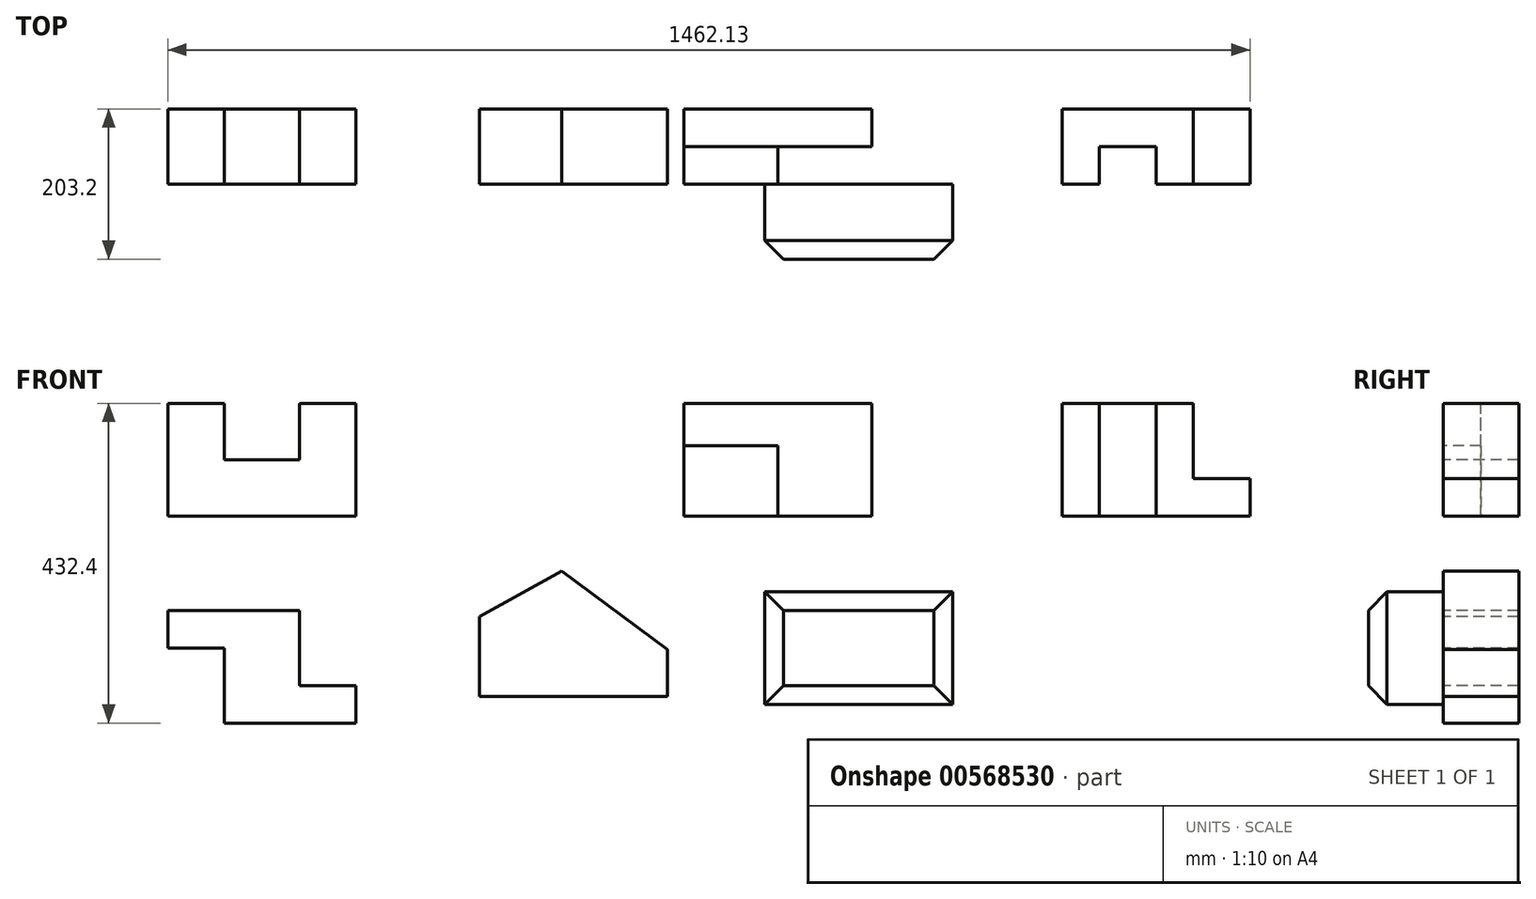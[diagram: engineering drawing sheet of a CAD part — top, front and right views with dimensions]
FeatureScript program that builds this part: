
annotation { "Feature Type Name" : "Feature", "Feature Type Description" : "" }
export const myFeature = defineFeature(function(context is Context, id is Id, definition is map)
    precondition{}
    {
        {
            var Q0;
            Q0=qCreatedBy(makeId("Front.planeOp"),FACE);
            var sketch = newSketch(context, id + "F0", { "sketchPlane" : qUnion([Q0])});
            skLineSegment(sketch, "E0", {"start": v(0, 0) * mm, "end": v(254, 0) * mm});
            skLineSegment(sketch, "E1", {"start": v(254, 0) * mm, "end": v(254, 152.4) * mm});
            skLineSegment(sketch, "E2", {"start": v(254, 152.4) * mm, "end": v(177.8, 152.4) * mm});
            skLineSegment(sketch, "E3", {"start": v(177.8, 152.4) * mm, "end": v(177.8, 76.2) * mm});
            skLineSegment(sketch, "E4", {"start": v(177.8, 76.2) * mm, "end": v(76.2, 76.2) * mm});
            skLineSegment(sketch, "E5", {"start": v(76.2, 76.2) * mm, "end": v(76.2, 152.4) * mm});
            skLineSegment(sketch, "E6", {"start": v(76.2, 152.4) * mm, "end": v(0, 152.4) * mm});
            skLineSegment(sketch, "E7", {"start": v(0, 152.4) * mm, "end": v(0, 0) * mm});
            skSolve(sketch);
        }
        {
            var Q0;
            Q0=makeQuery(id+"F0.imprint","IMPRINT",FACE,{"disambiguationData":[TD([[makeQuery(id+"F0.imprint","IMPRINT",EDGE,{"derivedFrom":sQuery(id+"F0.wireOp",EDGE,"E0")}),1.0]])]});
            extrude(context, id + "F1", {"entities" : qUnion([Q0]), "oppositeDirection" : true, "depth" : 101.6 * mm, "offsetDistance" : 25.4 * mm});
        }
        {
            var Q0;
            Q0=qCreatedBy(makeId("Front.planeOp"),FACE);
            var sketch = newSketch(context, id + "F2", { "sketchPlane" : qUnion([Q0])});
            skLineSegment(sketch, "E8.bottom", {"start": v(697.05, 0) * mm, "end": v(951.05, 0) * mm});
            skLineSegment(sketch, "E8.top", {"start": v(697.05, 152.4) * mm, "end": v(951.05, 152.4) * mm});
            skLineSegment(sketch, "E8.left", {"start": v(697.05, 0) * mm, "end": v(697.05, 152.4) * mm});
            skLineSegment(sketch, "E8.right", {"start": v(951.05, 0) * mm, "end": v(951.05, 152.4) * mm});
            skSolve(sketch);
        }
        {
            var Q0;
            Q0=makeQuery(id+"F2.imprint","IMPRINT",FACE,{"disambiguationData":[TD([[makeQuery(id+"F2.imprint","IMPRINT",EDGE,{"derivedFrom":sQuery(id+"F2.wireOp",EDGE,"E8.bottom")}),1.0]])]});
            extrude(context, id + "F3", {"entities" : qUnion([Q0]), "oppositeDirection" : true, "depth" : 101.6 * mm, "offsetDistance" : 25.4 * mm});
        }
        {
            var Q0;
            Q0=makeQuery(id+"F3.opExtrude","CAP_FACE",FACE,{"disambiguationData":[OSD([sQuery(id+"F2.wireOp",EDGE,"E8.bottom"),sQuery(id+"F2.wireOp",EDGE,"E8.top"),sQuery(id+"F2.wireOp",EDGE,"E8.left"),sQuery(id+"F2.wireOp",EDGE,"E8.right")])],"isStart":true});
            var sketch = newSketch(context, id + "F4", { "sketchPlane" : qUnion([Q0])});
            skLineSegment(sketch, "E9", {"start": v(951.05, 0) * mm, "end": v(951.05, 152.4) * mm});
            skLineSegment(sketch, "E10", {"start": v(951.05, 152.4) * mm, "end": v(697.05, 152.4) * mm});
            skLineSegment(sketch, "E11", {"start": v(824.05, 101.6) * mm, "end": v(824.05, 0) * mm});
            skLineSegment(sketch, "E12", {"start": v(697.05, 95.19) * mm, "end": v(824.05, 95.19) * mm});
            skSolve(sketch);
        }
        {
            var Q0;
            {var subQ5=sQuery(id+"F4.wireOp",EDGE,"E9");Q0=makeQuery(id+"F4.imprint","IMPRINT",FACE,{"disambiguationData":[TD([[makeQuery(id+"F4.imprint","IMPRINT",EDGE,{"derivedFrom":subQ5}),1.0]])]});}
            extrude(context, id + "F5", {"entities" : qUnion([Q0]), "operationType" : NewBodyOperationType.REMOVE, "oppositeDirection" : true, "depth" : 50.8 * mm, "offsetDistance" : 25.4 * mm});
        }
        {
            var Q0;
            Q0=qCreatedBy(makeId("Front.planeOp"),FACE);
            var sketch = newSketch(context, id + "F6", { "sketchPlane" : qUnion([Q0])});
            skLineSegment(sketch, "E13", {"start": v(1208.13, 0) * mm, "end": v(1462.13, 0) * mm});
            skLineSegment(sketch, "E14", {"start": v(1462.13, 0) * mm, "end": v(1462.13, 50.8) * mm});
            skLineSegment(sketch, "E15", {"start": v(1462.13, 50.8) * mm, "end": v(1385.93, 50.8) * mm});
            skLineSegment(sketch, "E16", {"start": v(1385.93, 50.8) * mm, "end": v(1385.93, 152.4) * mm});
            skLineSegment(sketch, "E17", {"start": v(1385.93, 152.4) * mm, "end": v(1208.13, 152.4) * mm});
            skLineSegment(sketch, "E18", {"start": v(1208.13, 152.4) * mm, "end": v(1208.13, 0) * mm});
            skSolve(sketch);
        }
        {
            var Q0;
            Q0=makeQuery(id+"F6.imprint","IMPRINT",FACE,{"disambiguationData":[TD([[makeQuery(id+"F6.imprint","IMPRINT",EDGE,{"derivedFrom":sQuery(id+"F6.wireOp",EDGE,"E13")}),1.0]])]});
            extrude(context, id + "F7", {"entities" : qUnion([Q0]), "oppositeDirection" : true, "depth" : 101.6 * mm, "offsetDistance" : 25.4 * mm});
        }
        {
            var Q0;
            Q0=makeQuery(id+"F7.opExtrude","SWEPT_FACE",FACE,{"disambiguationData":[OSD([sQuery(id+"F6.wireOp",EDGE,"E17")])]});
            var sketch = newSketch(context, id + "F8", { "sketchPlane" : qUnion([Q0])});
            skLineSegment(sketch, "E19", {"start": v(1208.13, 0) * mm, "end": v(1258.93, 0) * mm});
            skLineSegment(sketch, "E20", {"start": v(1258.93, 0) * mm, "end": v(1258.93, 50.8) * mm});
            skLineSegment(sketch, "E21", {"start": v(1258.93, 50.8) * mm, "end": v(1335.13, 50.8) * mm});
            skLineSegment(sketch, "E22", {"start": v(1335.13, 50.8) * mm, "end": v(1335.13, 0) * mm});
            skLineSegment(sketch, "E23", {"start": v(1335.13, 0) * mm, "end": v(1258.93, 0) * mm});
            skSolve(sketch);
        }
        {
            var Q0;
            Q0=makeQuery(id+"F8.imprint","IMPRINT",FACE,{"disambiguationData":[TD([[makeQuery(id+"F8.imprint","IMPRINT",EDGE,{"derivedFrom":sQuery(id+"F8.wireOp",EDGE,"E20")}),-1.0]])]});
            extrude(context, id + "F9", {"entities" : qUnion([Q0]), "operationType" : NewBodyOperationType.REMOVE, "oppositeDirection" : true, "depth" : 152.4 * mm, "offsetDistance" : 25.4 * mm});
        }
        {
            var Q0;
            Q0=qCreatedBy(makeId("Front.planeOp"),FACE);
            var sketch = newSketch(context, id + "F10", { "sketchPlane" : qUnion([Q0])});
            skLineSegment(sketch, "E24", {"start": v(0, -178.4) * mm, "end": v(76.2, -178.4) * mm});
            skLineSegment(sketch, "E25", {"start": v(76.2, -178.4) * mm, "end": v(76.2, -280) * mm});
            skLineSegment(sketch, "E26", {"start": v(76.2, -280) * mm, "end": v(254, -280) * mm});
            skLineSegment(sketch, "E27", {"start": v(254, -280) * mm, "end": v(254, -229.2) * mm});
            skLineSegment(sketch, "E28", {"start": v(254, -229.2) * mm, "end": v(177.8, -229.2) * mm});
            skLineSegment(sketch, "E29", {"start": v(177.8, -229.2) * mm, "end": v(177.8, -127.6) * mm});
            skLineSegment(sketch, "E30", {"start": v(177.8, -127.6) * mm, "end": v(0, -127.6) * mm});
            skLineSegment(sketch, "E31", {"start": v(0, -127.6) * mm, "end": v(0, -178.4) * mm});
            skSolve(sketch);
        }
        {
            var Q0;
            Q0=makeQuery(id+"F10.imprint","IMPRINT",FACE,{"disambiguationData":[TD([[makeQuery(id+"F10.imprint","IMPRINT",EDGE,{"derivedFrom":sQuery(id+"F10.wireOp",EDGE,"E24")}),1.0]])]});
            extrude(context, id + "F11", {"entities" : qUnion([Q0]), "oppositeDirection" : true, "depth" : 101.6 * mm, "offsetDistance" : 25.4 * mm});
        }
        {
            var Q0;
            Q0=qCreatedBy(makeId("Front.planeOp"),FACE);
            var sketch = newSketch(context, id + "F12", { "sketchPlane" : qUnion([Q0])});
            skLineSegment(sketch, "E32", {"start": v(420.88, -243.97) * mm, "end": v(674.88, -243.97) * mm});
            skLineSegment(sketch, "E33", {"start": v(420.88, -243.97) * mm, "end": v(420.88, -136.02) * mm});
            skLineSegment(sketch, "E34", {"start": v(420.88, -136.02) * mm, "end": v(532.04, -74.6) * mm});
            skLineSegment(sketch, "E35", {"start": v(532.04, -74.6) * mm, "end": v(674.88, -180.47) * mm});
            skLineSegment(sketch, "E36", {"start": v(674.88, -180.47) * mm, "end": v(674.88, -243.97) * mm});
            skSolve(sketch);
        }
        {
            var Q0;
            Q0=makeQuery(id+"F12.imprint","IMPRINT",FACE,{"disambiguationData":[TD([[makeQuery(id+"F12.imprint","IMPRINT",EDGE,{"derivedFrom":sQuery(id+"F12.wireOp",EDGE,"E32")}),1.0]])]});
            extrude(context, id + "F13", {"entities" : qUnion([Q0]), "oppositeDirection" : true, "depth" : 101.6 * mm, "offsetDistance" : 25.4 * mm});
        }
        {
            var Q0;
            Q0=qCreatedBy(makeId("Front.planeOp"),FACE);
            var sketch = newSketch(context, id + "F14", { "sketchPlane" : qUnion([Q0])});
            skLineSegment(sketch, "E37", {"start": v(806.61, -254.85) * mm, "end": v(1060.61, -254.85) * mm});
            skLineSegment(sketch, "E38", {"start": v(806.61, -102.45) * mm, "end": v(1060.61, -102.45) * mm});
            skLineSegment(sketch, "E39", {"start": v(1060.61, -102.45) * mm, "end": v(1060.61, -254.85) * mm});
            skLineSegment(sketch, "E40", {"start": v(806.61, -254.85) * mm, "end": v(806.61, -102.45) * mm});
            skSolve(sketch);
        }
        {
            var Q0;
            Q0=makeQuery(id+"F14.imprint","IMPRINT",FACE,{"disambiguationData":[TD([[makeQuery(id+"F14.imprint","IMPRINT",EDGE,{"derivedFrom":sQuery(id+"F14.wireOp",EDGE,"E37")}),1.0]])]});
            extrude(context, id + "F15", {"entities" : qUnion([Q0]), "depth" : 101.6 * mm, "offsetDistance" : 25.4 * mm});
        }
        {
            var Q0;
            Q0=makeQuery(id+"F15.opExtrude","CAP_FACE",FACE,{"disambiguationData":[OSD([sQuery(id+"F14.wireOp",EDGE,"E37"),sQuery(id+"F14.wireOp",EDGE,"E38"),sQuery(id+"F14.wireOp",EDGE,"E39"),sQuery(id+"F14.wireOp",EDGE,"E40")])],"isStart":false});
            chamfer(context, id + "F16", {"entities" : qUnion([Q0]), "width" : 25.4 * mm, "tangentPropagation" : true});
        }
    });
